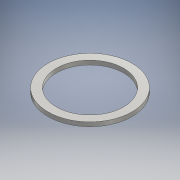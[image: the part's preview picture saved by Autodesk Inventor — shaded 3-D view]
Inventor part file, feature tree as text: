
AUTODESK INVENTOR PART (.ipt)
format: ipt  version: 2016 (Build 200138000, 138)  size: 99,328 bytes
history: native  units: mm
features: other x1, extrude x1, sketch x1
ambient origin geometry x8: Origin, YZ Plane, XZ Plane, XY Plane, X Axis, Y Axis, Z Axis, Center Point
bodies: Body1 (feature_tree)
feature tree (3):
  other  "ソリッド1"
  extrude  "押し出し1"  Depth=8.0mm
  sketch  "スケッチ1"
